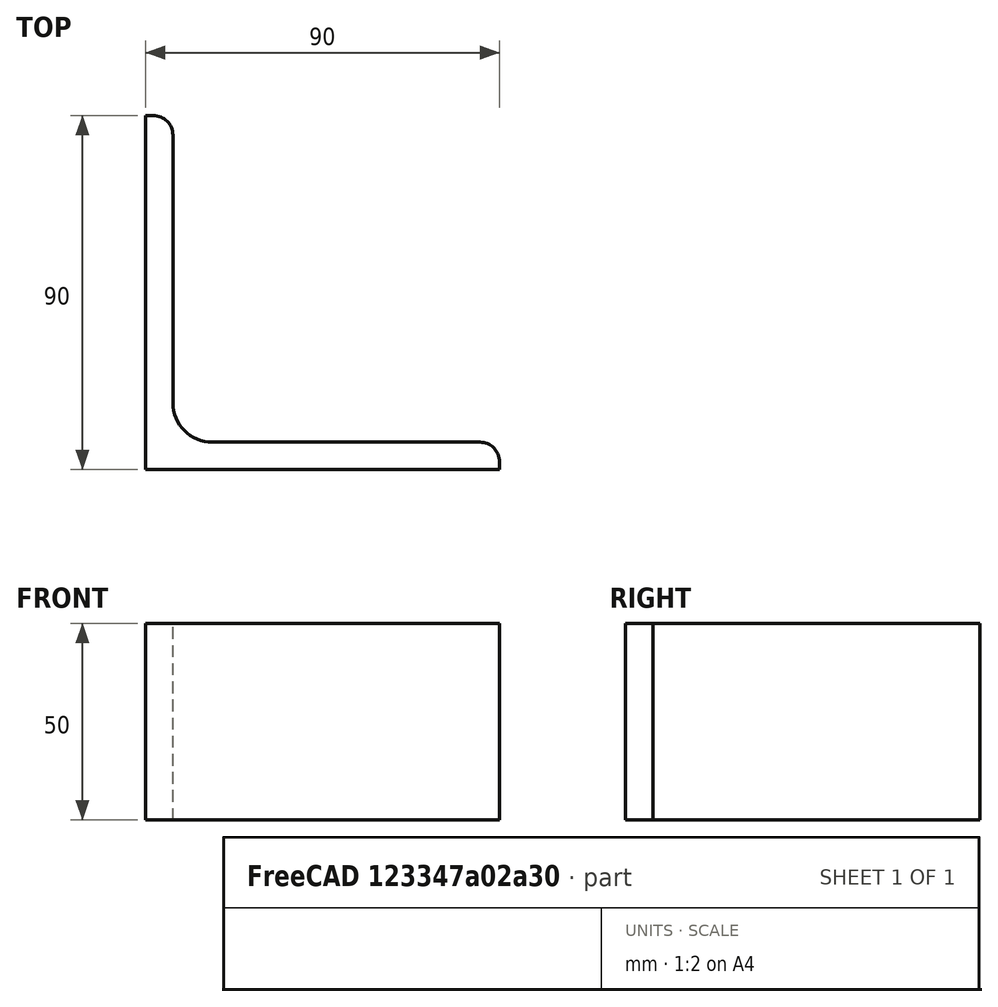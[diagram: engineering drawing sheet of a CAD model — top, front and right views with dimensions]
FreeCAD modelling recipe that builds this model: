
FCSTD DOCUMENT  (FreeCAD 0.15R4671 (Git))
Label: Angle Bar L90x90x7 EN10056 S235JR
License: All rights reserved
LicenseURL: http://en.wikipedia.org/wiki/All_rights_reserved
objects: Sketcher::SketchObject×1, Part::Extrusion×1
note: 2 computed .brp shape members not serialized (recipe doc carries the construction recipe); baked Part::Feature solids carry a one-line shape summary decoded from their .brp

FEATURE [Sketcher::SketchObject] Sketch
  sketch-geometry (9):
    g0: LineSegment StartX=0 StartY=0 StartZ=0 EndX=90 EndY=0 EndZ=0
    g1: LineSegment StartX=90 StartY=0 StartZ=0 EndX=90 EndY=2 EndZ=0
    g2: LineSegment StartX=85 StartY=7 StartZ=0 EndX=17 EndY=7 EndZ=0
    g3: LineSegment StartX=0 StartY=0 StartZ=0 EndX=0 EndY=90 EndZ=0
    g4: LineSegment StartX=0 StartY=90 StartZ=0 EndX=2 EndY=90 EndZ=0
    g5: LineSegment StartX=7 StartY=85 StartZ=0 EndX=7 EndY=17 EndZ=0
    g6: ArcOfCircle CenterX=17 CenterY=17 CenterZ=0 NormalX=0 NormalY=0 NormalZ=1 Radius=10 StartAngle=3.14159 EndAngle=4.71239
    g7: ArcOfCircle CenterX=2 CenterY=85 CenterZ=0 NormalX=0 NormalY=0 NormalZ=1 Radius=5 StartAngle=0 EndAngle=1.5708
    g8: ArcOfCircle CenterX=85 CenterY=2 CenterZ=0 NormalX=0 NormalY=0 NormalZ=1 Radius=5 StartAngle=0 EndAngle=1.5708
  constraints (23):
    c: Coincident(g0,g-1)
    c: Horizontal(g0)
    c: Coincident(g1,g0)
    c: Vertical(g1)
    c: Horizontal(g2)
    c: Coincident(g3,g-1)
    c: Vertical(g3)
    c: Coincident(g4,g3)
    c: Horizontal(g4)
    c: Vertical(g5)
    c: Tangent(g5,g6) = -1.5708
    c: Tangent(g2,g6) = 1.5708
    c: Tangent(g4,g7) = 1.5708
    c: Tangent(g5,g7) = 1.5708
    c: Tangent(g2,g8) = -1.5708
    c: Tangent(g1,g8) = -1.5708
    c: DistanceX(g0) = 90
    c: DistanceY(g3) = 90
    c: DistanceY(g0,g2) = 7
    c: DistanceX(g3,g5) = 7
    c: Radius(g6) = 10
    c: Radius(g8) = 5
    c: Radius(g7) = 5
FEATURE [Part::Extrusion] Extrude  label="Angle Bar L90x90x7 EN10056 S235JR"
  Base = -> Sketch
  Dir = (0,0,50)
  Solid = true
